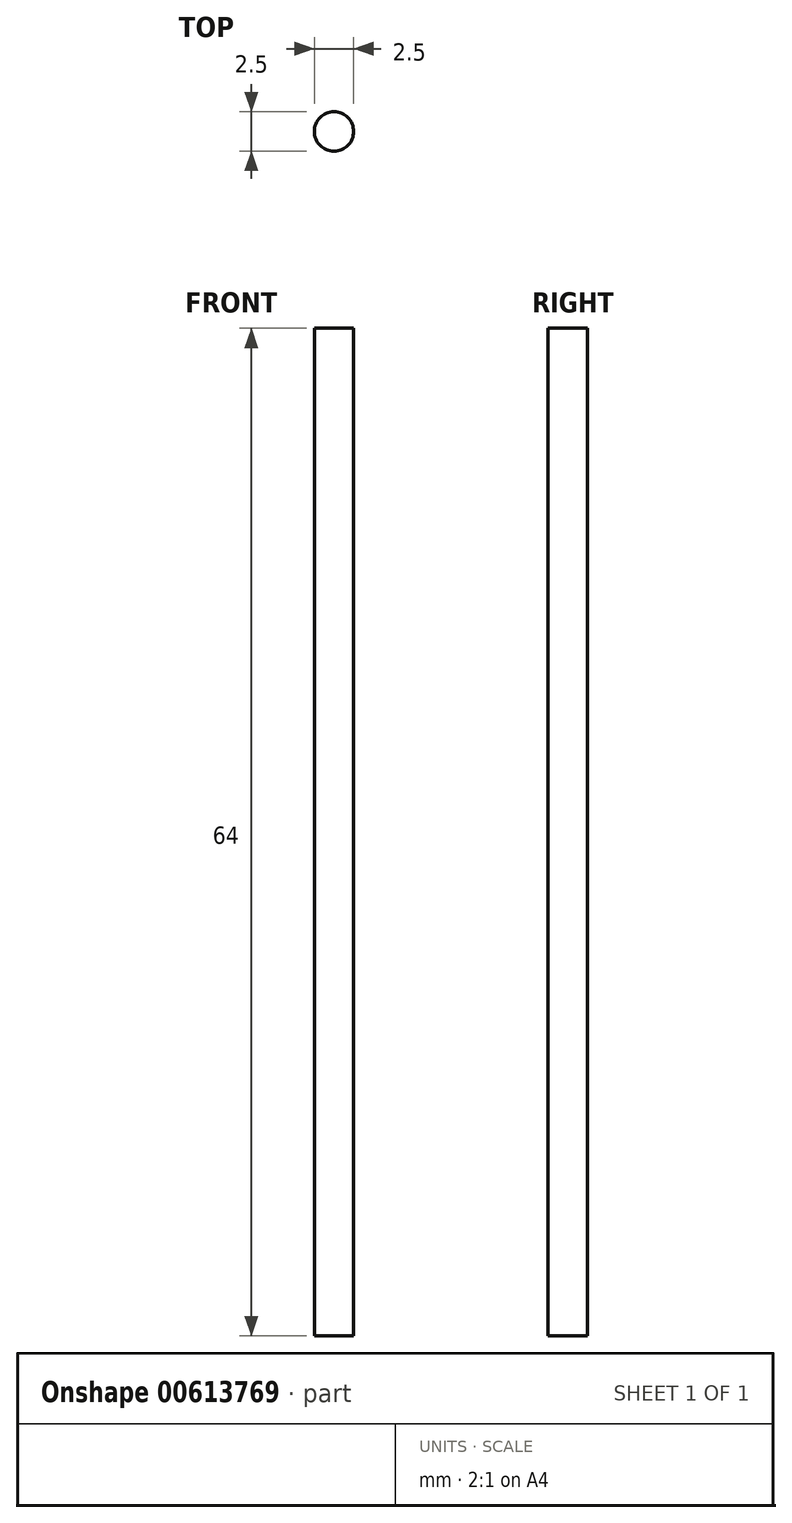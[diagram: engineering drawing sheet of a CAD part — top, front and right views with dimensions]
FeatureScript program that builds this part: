
annotation { "Feature Type Name" : "Feature", "Feature Type Description" : "" }
export const myFeature = defineFeature(function(context is Context, id is Id, definition is map)
    precondition{}
    {
        {
            var Q0;
            Q0=qCreatedBy(makeId("Top.planeOp"),FACE);
            var sketch = newSketch(context, id + "F0", { "sketchPlane" : qUnion([Q0])});
            skCircle(sketch, "E0", {"center": v(0, 0) * mm, "radius": 1.25 * mm});
            skSolve(sketch);
        }
        {
            var Q0;
            Q0=qSketchRegion(id+"F0",true);
            extrude(context, id + "F1", {"entities" : qUnion([Q0]), "depth" : 64 * mm, "offsetDistance" : 25.4 * mm});
        }
    });
